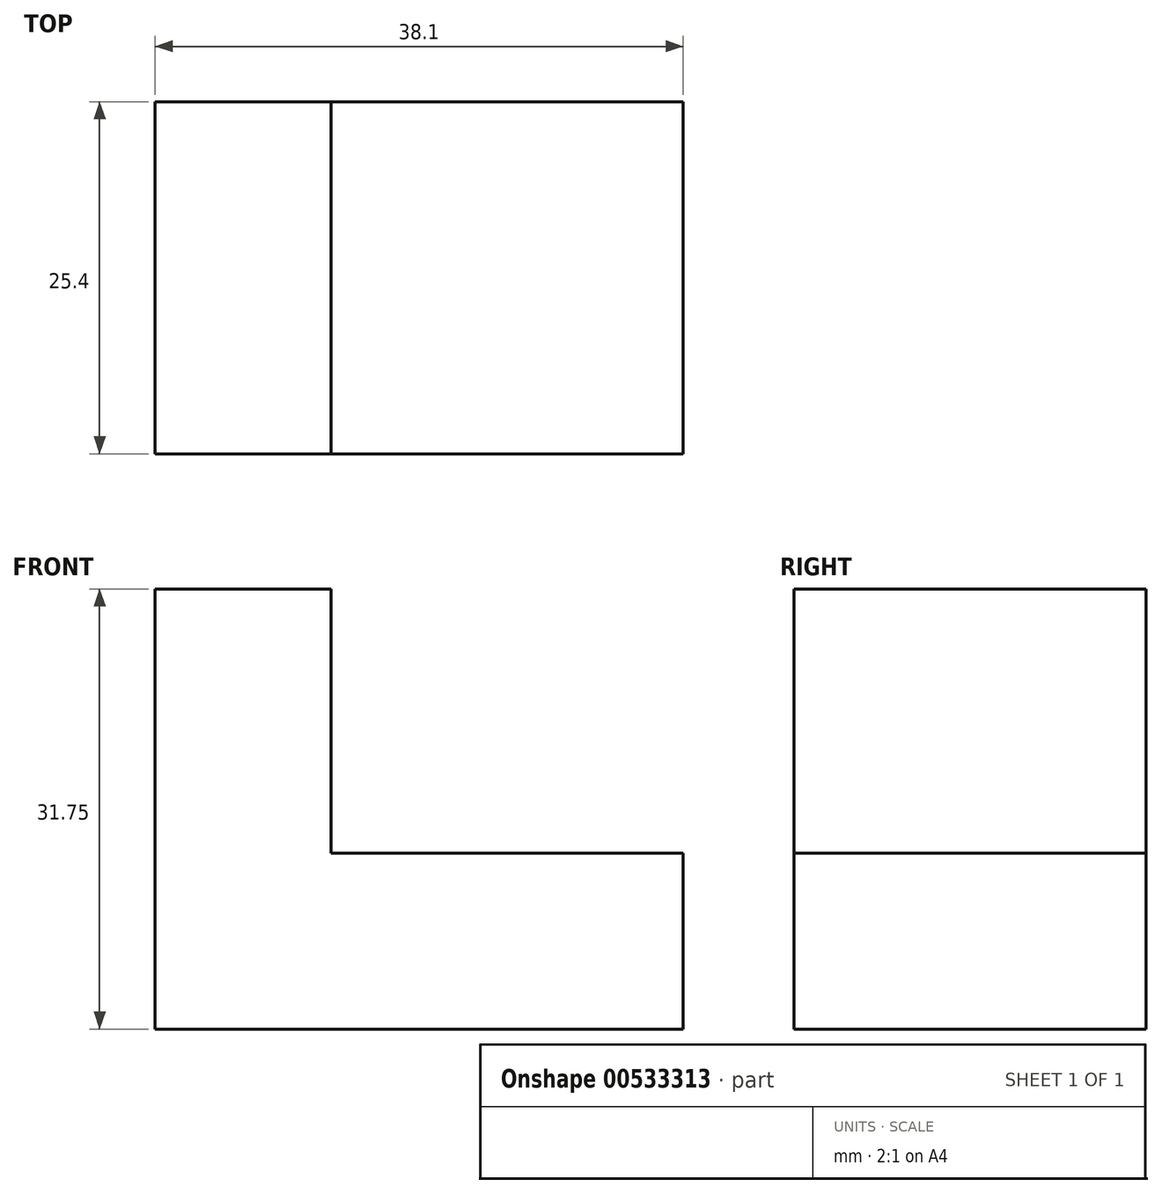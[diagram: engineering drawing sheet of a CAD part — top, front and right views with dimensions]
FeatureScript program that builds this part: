
annotation { "Feature Type Name" : "Feature", "Feature Type Description" : "" }
export const myFeature = defineFeature(function(context is Context, id is Id, definition is map)
    precondition{}
    {
        {
            var Q0;
            Q0=qCreatedBy(makeId("Front.planeOp"),FACE);
            var sketch = newSketch(context, id + "F0", { "sketchPlane" : qUnion([Q0])});
            skLineSegment(sketch, "E0", {"start": v(0, 0) * mm, "end": v(0, 31.75) * mm});
            skLineSegment(sketch, "E1", {"start": v(0, 31.75) * mm, "end": v(12.7, 31.75) * mm});
            skLineSegment(sketch, "E2", {"start": v(0, 0) * mm, "end": v(38.1, 0) * mm});
            skLineSegment(sketch, "E3", {"start": v(12.7, 31.75) * mm, "end": v(12.7, 12.7) * mm});
            skLineSegment(sketch, "E4", {"start": v(12.7, 12.7) * mm, "end": v(38.1, 12.7) * mm});
            skLineSegment(sketch, "E5", {"start": v(38.1, 0) * mm, "end": v(38.1, 12.7) * mm});
            skSolve(sketch);
        }
        {
            var Q0;
            Q0 = qSketchRegion(id + "F0", true);
            extrude(context, id + "F1", {"entities" : qUnion([Q0]), "depth" : 25.4 * mm, "offsetDistance" : 25.4 * mm});
        }
    });
